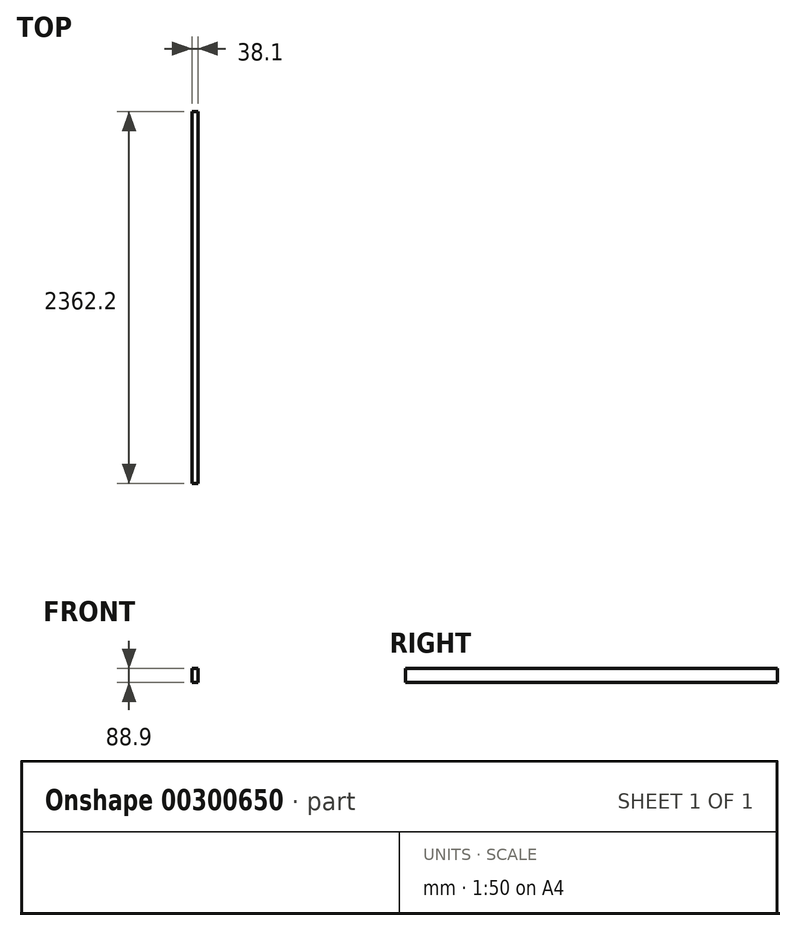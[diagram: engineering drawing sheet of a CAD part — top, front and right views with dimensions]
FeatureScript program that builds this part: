
annotation { "Feature Type Name" : "Feature", "Feature Type Description" : "" }
export const myFeature = defineFeature(function(context is Context, id is Id, definition is map)
    precondition{}
    {
        {
            var Q0;
            Q0=qCreatedBy(makeId("Front.planeOp"),FACE);
            var sketch = newSketch(context, id + "F0", { "sketchPlane" : qUnion([Q0])});
            skLineSegment(sketch, "E0.bottom", {"start": v(0, 0) * mm, "end": v(38.1, 0) * mm});
            skLineSegment(sketch, "E0.top", {"start": v(0, 88.9) * mm, "end": v(38.1, 88.9) * mm});
            skLineSegment(sketch, "E0.left", {"start": v(0, 0) * mm, "end": v(0, 88.9) * mm});
            skLineSegment(sketch, "E0.right", {"start": v(38.1, 0) * mm, "end": v(38.1, 88.9) * mm});
            skSolve(sketch);
        }
        {
            var Q0;
            Q0 = qSketchRegion(id + "F0", true);
            extrude(context, id + "F1", {"entities" : qUnion([Q0]), "depth" : 2362.2 * mm});
        }
    });
